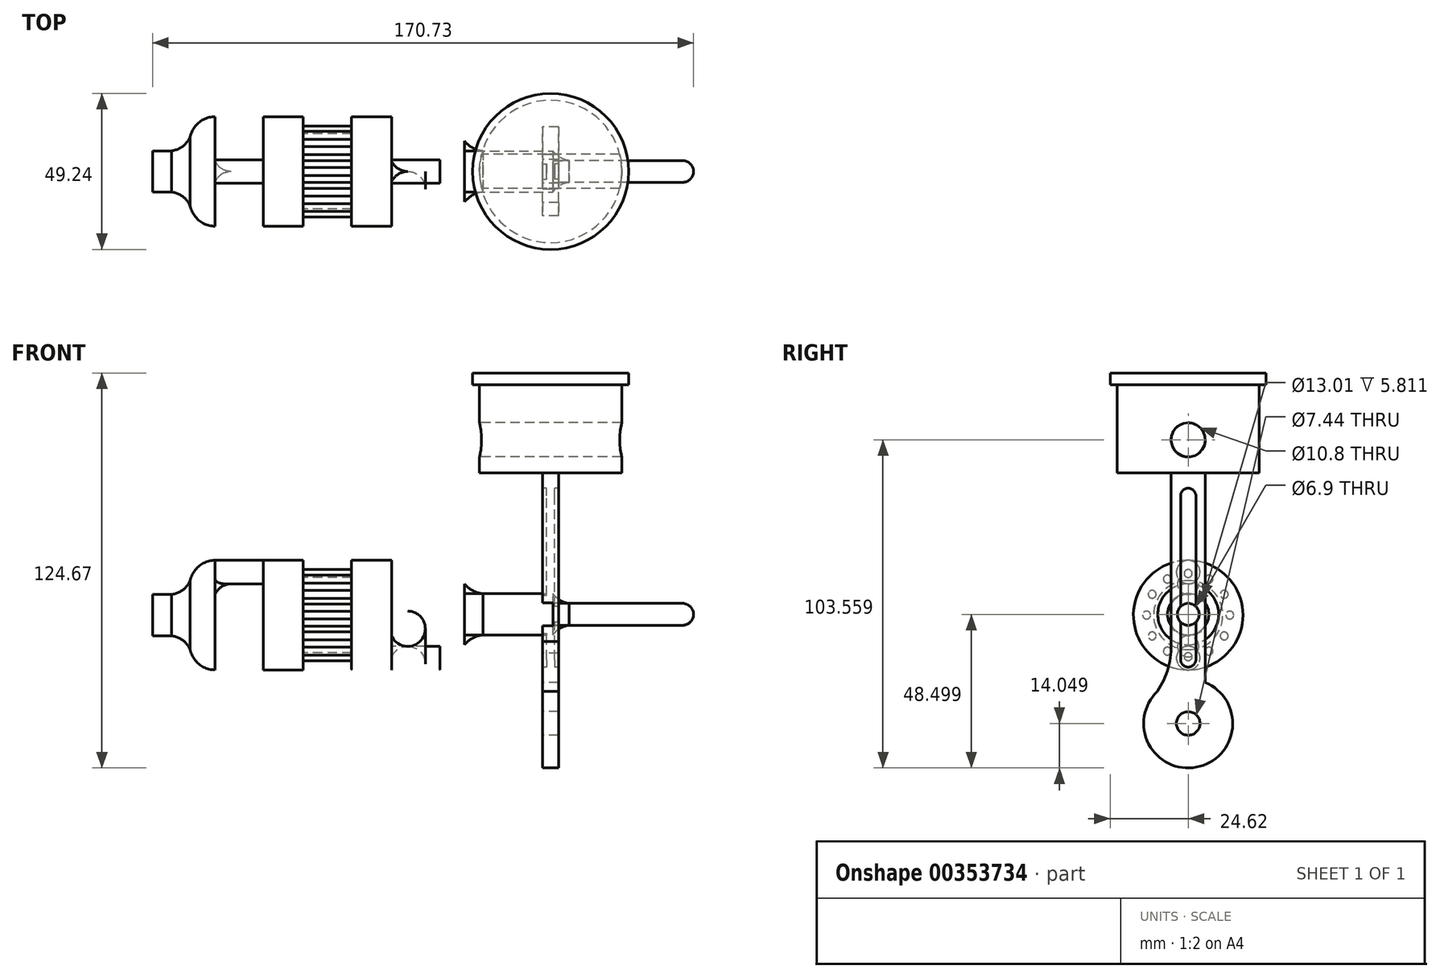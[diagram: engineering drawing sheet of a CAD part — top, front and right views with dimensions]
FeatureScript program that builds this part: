
annotation { "Feature Type Name" : "Feature", "Feature Type Description" : "" }
export const myFeature = defineFeature(function(context is Context, id is Id, definition is map)
    precondition{}
    {
        {
            var Q0;
            Q0=qCreatedBy(makeId("Front.planeOp"),FACE);
            var sketch = newSketch(context, id + "F0", { "sketchPlane" : qUnion([Q0])});
            skLineSegment(sketch, "E0.left", {"start": v(-105.92, 17.28) * mm, "end": v(-105.92, -17.28) * mm});
            skLineSegment(sketch, "E0.right", {"start": v(-113.74, 10.9) * mm, "end": v(-113.74, -10.9) * mm});
            skPoint(sketch, "E0.middle", {"position": v(-109.83, 0) * mm});
            skLineSegment(sketch, "E1.bottom", {"start": v(-113.74, 6.5) * mm, "end": v(-125.64, 6.5) * mm});
            skLineSegment(sketch, "E1.top", {"start": v(-113.74, -6.5) * mm, "end": v(-125.64, -6.5) * mm});
            skLineSegment(sketch, "E1.left", {"start": v(-113.74, 6.5) * mm, "end": v(-113.74, -6.5) * mm});
            skLineSegment(sketch, "E1.right", {"start": v(-125.64, 6.5) * mm, "end": v(-125.64, -6.5) * mm});
            skPoint(sketch, "E1.middle", {"position": v(-119.69, 0) * mm});
            skPoint(sketch, "E1.middle.positionSnap0", {"position": v(-113.74, 0) * mm});
            skPoint(sketch, "E1.centerSnap0", {"position": v(-113.74, 0) * mm});
            skLineSegment(sketch, "E2.bottom", {"start": v(-105.92, 17.28) * mm, "end": v(-90.68, 17.28) * mm});
            skLineSegment(sketch, "E2.top", {"start": v(-105.92, 9.85) * mm, "end": v(-90.68, 9.85) * mm});
            skLineSegment(sketch, "E2.left", {"start": v(-105.92, 17.28) * mm, "end": v(-105.92, 9.85) * mm});
            skLineSegment(sketch, "E2.right", {"start": v(-90.68, 17.28) * mm, "end": v(-90.68, 9.85) * mm});
            skPoint(sketch, "E2.middle", {"position": v(-98.3, 13.57) * mm});
            skLineSegment(sketch, "E3.bottom", {"start": v(-90.68, 17.28) * mm, "end": v(-78.06, 17.28) * mm});
            skLineSegment(sketch, "E3.top", {"start": v(-90.68, -17.28) * mm, "end": v(-78.06, -17.28) * mm});
            skLineSegment(sketch, "E3.left", {"start": v(-90.68, 17.28) * mm, "end": v(-90.68, -17.28) * mm});
            skLineSegment(sketch, "E3.right", {"start": v(-78.06, 17.28) * mm, "end": v(-78.06, -17.28) * mm});
            skPoint(sketch, "E3.middle", {"position": v(-84.37, 0) * mm});
            skLineSegment(sketch, "E4.bottom", {"start": v(-78.06, 3.45) * mm, "end": v(-62.82, 3.45) * mm});
            skLineSegment(sketch, "E4.top", {"start": v(-78.06, -3.98) * mm, "end": v(-62.82, -3.98) * mm});
            skLineSegment(sketch, "E4.left", {"start": v(-78.06, 3.45) * mm, "end": v(-78.06, -3.98) * mm});
            skLineSegment(sketch, "E4.right", {"start": v(-62.82, 3.45) * mm, "end": v(-62.82, -3.98) * mm});
            skPoint(sketch, "E4.middle", {"position": v(-70.44, -0.27) * mm});
            skLineSegment(sketch, "E5.right", {"start": v(-62.82, 17.28) * mm, "end": v(-62.82, 9.85) * mm});
            skLineSegment(sketch, "E6.bottom", {"start": v(-62.82, 17.28) * mm, "end": v(-50.23, 17.28) * mm});
            skLineSegment(sketch, "E6.top", {"start": v(-62.82, -17.28) * mm, "end": v(-50.23, -17.28) * mm});
            skLineSegment(sketch, "E6.left", {"start": v(-62.82, 17.28) * mm, "end": v(-62.82, -17.28) * mm});
            skLineSegment(sketch, "E6.right", {"start": v(-50.23, 17.28) * mm, "end": v(-50.23, -17.28) * mm});
            skPoint(sketch, "E6.middle", {"position": v(-56.53, 0) * mm});
            skLineSegment(sketch, "E7.bottom", {"start": v(-50.23, -9.85) * mm, "end": v(-34.94, -9.85) * mm});
            skLineSegment(sketch, "E7.top", {"start": v(-50.23, -17.28) * mm, "end": v(-34.94, -17.28) * mm});
            skLineSegment(sketch, "E7.left", {"start": v(-50.23, -9.85) * mm, "end": v(-50.23, -17.28) * mm});
            skPoint(sketch, "E7.middle", {"position": v(-42.59, -13.57) * mm});
            skLineSegment(sketch, "E8.bottom", {"start": v(-27.13, 6.75) * mm, "end": v(0.74, 6.75) * mm});
            skLineSegment(sketch, "E8.top", {"start": v(-27.13, -6.26) * mm, "end": v(0.74, -6.26) * mm});
            skLineSegment(sketch, "E8.right", {"start": v(0.74, 6.75) * mm, "end": v(0.74, -6.26) * mm});
            skPoint(sketch, "E8.middle", {"position": v(-13.2, 0.25) * mm});
            skLineSegment(sketch, "E9.left", {"start": v(0.74, 3.7) * mm, "end": v(0.74, -3.2) * mm});
            skLineSegment(sketch, "E10.left", {"start": v(-27.13, 10.99) * mm, "end": v(-27.13, -10.99) * mm});
            skLineSegment(sketch, "E10.right", {"start": v(-34.94, 17.28) * mm, "end": v(-34.94, -17.28) * mm});
            skPoint(sketch, "E10.middle", {"position": v(-31.04, 0) * mm});
            skPoint(sketch, "E11.middle.positionSnap0", {"position": v(-34.94, 0) * mm});
            skPoint(sketch, "E11.centerSnap0", {"position": v(-34.94, 0) * mm});
            skLineSegment(sketch, "E12.left", {"start": v(-27.13, 10.99) * mm, "end": v(-27.13, 9.85) * mm});
            skLineSegment(sketch, "E13", {"start": v(-105.92, 0) * mm, "end": v(-125.64, 0) * mm});
            skLineSegment(sketch, "E14", {"start": v(-105.92, 13.57) * mm, "end": v(-90.68, 13.57) * mm});
            skLineSegment(sketch, "E15", {"start": v(-90.68, 0) * mm, "end": v(-78.06, 0) * mm});
            skLineSegment(sketch, "E16", {"start": v(-78.06, 0) * mm, "end": v(-50.23, 0) * mm});
            skLineSegment(sketch, "E17", {"start": v(-50.23, -13.57) * mm, "end": v(-34.94, -13.57) * mm});
            skLineSegment(sketch, "E18", {"start": v(-13.2, 0.25) * mm, "end": v(0.74, 0.25) * mm});
            skLineSegment(sketch, "E19", {"start": v(-27.13, 0) * mm, "end": v(-31.04, 0) * mm});
            skLineSegment(sketch, "E20", {"start": v(-34.94, 0) * mm, "end": v(-31.04, 0) * mm});
            skLineSegment(sketch, "E21", {"start": v(-13.2, 0.25) * mm, "end": v(-27.13, 0.25) * mm});
            skLineSegment(sketch, "E22.bottom", {"start": v(0.74, 3.7) * mm, "end": v(41.64, 3.7) * mm});
            skLineSegment(sketch, "E22.top", {"start": v(0.74, -3.2) * mm, "end": v(41.64, -3.2) * mm});
            skLineSegment(sketch, "E22.right", {"start": v(41.64, 3.7) * mm, "end": v(41.64, -3.2) * mm});
            skPoint(sketch, "E22.middle", {"position": v(21.2, 0.25) * mm});
            skLineSegment(sketch, "E23", {"start": v(0.74, 0.25) * mm, "end": v(21.2, 0.25) * mm});
            skLineSegment(sketch, "E24", {"start": v(21.2, 0.25) * mm, "end": v(41.64, 0.25) * mm});
            skLineSegment(sketch, "E25.bottom", {"start": v(-95.76, 9.85) * mm, "end": v(-100.84, 9.85) * mm});
            skLineSegment(sketch, "E25.top", {"start": v(-95.76, 17.28) * mm, "end": v(-100.84, 17.28) * mm});
            skLineSegment(sketch, "E25.left", {"start": v(-95.76, 9.85) * mm, "end": v(-95.76, 17.28) * mm});
            skLineSegment(sketch, "E25.right", {"start": v(-100.84, 9.85) * mm, "end": v(-100.84, 17.28) * mm});
            skLineSegment(sketch, "E26.bottom", {"start": v(-40.05, -17.28) * mm, "end": v(-45.13, -17.28) * mm});
            skLineSegment(sketch, "E26.top", {"start": v(-40.05, -9.85) * mm, "end": v(-45.13, -9.85) * mm});
            skLineSegment(sketch, "E26.left", {"start": v(-40.05, -17.28) * mm, "end": v(-40.05, -9.85) * mm});
            skLineSegment(sketch, "E26.right", {"start": v(-45.13, -17.28) * mm, "end": v(-45.13, -9.85) * mm});
            skArc(sketch, "E27", {"start": v(-100.84, 9.85) * mm, "mid": v(-103.88, 8.94) * mm, "end": v(-105.92, 6.5) * mm});
            skLineSegment(sketch, "E28", {"start": v(-98.3, 9.85) * mm, "end": v(-98.3, 17.28) * mm});
            skArc(sketch, "E29.MirrorCS", {"start": v(-95.76, 9.85) * mm, "mid": v(-92.72, 8.94) * mm, "end": v(-90.68, 6.5) * mm});
            skArc(sketch, "E30", {"start": v(-50.23, -6.5) * mm, "mid": v(-48.18, -8.94) * mm, "end": v(-45.13, -9.85) * mm});
            skLineSegment(sketch, "E31", {"start": v(-42.59, -17.28) * mm, "end": v(-42.59, -9.85) * mm});
            skArc(sketch, "E32.MirrorCS", {"start": v(-34.94, -6.5) * mm, "mid": v(-37, -8.94) * mm, "end": v(-40.05, -9.85) * mm});
            skLineSegment(sketch, "E33", {"start": v(-78.06, -0.27) * mm, "end": v(-62.82, -0.27) * mm});
            skArc(sketch, "E34", {"start": v(-27.13, 9.85) * mm, "mid": v(-24.56, 7.69) * mm, "end": v(-21.32, 6.75) * mm});
            skArc(sketch, "E35.MirrorCS", {"start": v(-27.13, -9.35) * mm, "mid": v(-24.56, -7.19) * mm, "end": v(-21.32, -6.26) * mm});
            skArc(sketch, "E36", {"start": v(0.74, 6.75) * mm, "mid": v(2.97, 4.68) * mm, "end": v(5.86, 3.7) * mm});
            skArc(sketch, "E37", {"start": v(-119.69, 6.5) * mm, "mid": v(-116.13, 7.91) * mm, "end": v(-113.74, 10.9) * mm});
            skArc(sketch, "E38", {"start": v(-105.92, 17.28) * mm, "mid": v(-110.97, 15.49) * mm, "end": v(-113.74, 10.9) * mm});
            skArc(sketch, "E39.MirrorCS", {"start": v(-34.94, 17.28) * mm, "mid": v(-29.9, 15.48) * mm, "end": v(-27.12, 10.9) * mm});
            skPoint(sketch, "E40.orphan", {"position": v(-113.74, 17.28) * mm});
            skPoint(sketch, "E41.orphan", {"position": v(-27.13, 17.28) * mm});
            skArc(sketch, "E42.MirrorCS", {"start": v(-105.92, -17.28) * mm, "mid": v(-110.97, -15.49) * mm, "end": v(-113.74, -10.9) * mm});
            skArc(sketch, "E43.MirrorCS", {"start": v(-34.94, -17.28) * mm, "mid": v(-29.9, -15.48) * mm, "end": v(-27.12, -10.9) * mm});
            skPoint(sketch, "E44.orphan", {"position": v(-113.74, -17.28) * mm});
            skPoint(sketch, "E45.orphan", {"position": v(-27.13, -17.28) * mm});
            skLineSegment(sketch, "E46.bottom", {"start": v(-78.06, 14.38) * mm, "end": v(-62.82, 14.38) * mm});
            skLineSegment(sketch, "E46.top", {"start": v(-78.06, 11.89) * mm, "end": v(-62.82, 11.89) * mm});
            skLineSegment(sketch, "E46.left", {"start": v(-78.06, 14.38) * mm, "end": v(-78.06, 11.89) * mm});
            skLineSegment(sketch, "E46.right", {"start": v(-62.82, 14.38) * mm, "end": v(-62.82, 11.89) * mm});
            skLineSegment(sketch, "E47", {"start": v(-78.06, 13.13) * mm, "end": v(-62.82, 13.13) * mm});
            skArc(sketch, "E48", {"start": v(41.64, 3.7) * mm, "mid": v(45.09, 0.25) * mm, "end": v(41.64, -3.2) * mm});
            skLineSegment(sketch, "E49", {"start": v(41.64, 0.25) * mm, "end": v(45.09, 0.25) * mm});
            skSolve(sketch);
        }
        {
            var Q0;
            {var subQ0=sQuery(id+"F0.wireOp",EDGE,"E1.bottom");Q0=makeQuery(id+"F0.imprint","IMPRINT",FACE,{"disambiguationData":[TD([[makeQuery(id+"F0.imprint","IMPRINT",EDGE,{"derivedFrom":subQ0}),1.0]])]});}
            var Q1;
            {var subQ5=sQuery(id+"F0.wireOp",EDGE,"E0.bottom");Q1=makeQuery(id+"F0.imprint","IMPRINT",FACE,{"disambiguationData":[TD([[makeQuery(id+"F0.imprint","IMPRINT",EDGE,{"derivedFrom":subQ5}),1.0]])]});}
            var Q2;
            Q2=sQuery(id+"F0.wireOp",EDGE,"E13");
            revolve(context, id + "F1", {"entities" : qUnion([Q0, Q1]), "axis" : qUnion([Q2]), "revolveType" : RevolveType.FULL});
        }
        {
            var Q0;
            {var subQ0=sQuery(id+"F0.wireOp",EDGE,"E2.bottom");Q0=makeQuery(id+"F0.imprint","IMPRINT",FACE,{"disambiguationData":[TD([[makeQuery(id+"F0.imprint","IMPRINT",EDGE,{"derivedFrom":subQ0}),-1.0]])]});}
            var Q1;
            {var subQ5=sQuery(id+"F0.wireOp",EDGE,"E25.top");Q1=makeQuery(id+"F0.imprint","IMPRINT",FACE,{"disambiguationData":[TD([[makeQuery(id+"F0.imprint","IMPRINT",EDGE,{"derivedFrom":subQ5}),1.0]])]});}
            var Q2;
            Q2=sQuery(id+"F0.wireOp",EDGE,"E14");
            revolve(context, id + "F2", {"operationType" : NewBodyOperationType.ADD, "entities" : qUnion([Q0, Q1]), "axis" : qUnion([Q2]), "revolveType" : RevolveType.FULL});
        }
        {
            var Q0;
            {var subQ4=sQuery(id+"F0.wireOp",EDGE,"E3.bottom");Q0=makeQuery(id+"F0.imprint","IMPRINT",FACE,{"disambiguationData":[TD([[makeQuery(id+"F0.imprint","IMPRINT",EDGE,{"derivedFrom":subQ4}),-1.0]])]});}
            var Q1;
            {var subQ0=sQuery(id+"F0.wireOp",EDGE,"E4.bottom");Q1=makeQuery(id+"F0.imprint","IMPRINT",FACE,{"disambiguationData":[TD([[makeQuery(id+"F0.imprint","IMPRINT",EDGE,{"derivedFrom":subQ0}),-1.0]])]});}
            var Q2;
            {var subQ1=sQuery(id+"F0.wireOp",EDGE,"E6.bottom");Q2=makeQuery(id+"F0.imprint","IMPRINT",FACE,{"disambiguationData":[TD([[makeQuery(id+"F0.imprint","IMPRINT",EDGE,{"derivedFrom":subQ1}),-1.0]])]});}
            var Q3;
            Q3=sQuery(id+"F0.wireOp",EDGE,"E15");
            revolve(context, id + "F3", {"operationType" : NewBodyOperationType.ADD, "entities" : qUnion([Q0, Q1, Q2]), "axis" : qUnion([Q3]), "revolveType" : RevolveType.FULL});
        }
        {
            var Q0;
            {var subQ0=sQuery(id+"F0.wireOp",EDGE,"E7.bottom");Q0=makeQuery(id+"F0.imprint","IMPRINT",FACE,{"disambiguationData":[TD([[makeQuery(id+"F0.imprint","IMPRINT",EDGE,{"derivedFrom":subQ0}),-1.0]])]});}
            var Q1;
            {var subQ5=sQuery(id+"F0.wireOp",EDGE,"E26.top");Q1=makeQuery(id+"F0.imprint","IMPRINT",FACE,{"disambiguationData":[TD([[makeQuery(id+"F0.imprint","IMPRINT",EDGE,{"derivedFrom":subQ5}),1.0]])]});}
            var Q2;
            Q2=sQuery(id+"F0.wireOp",EDGE,"E17");
            revolve(context, id + "F4", {"operationType" : NewBodyOperationType.ADD, "entities" : qUnion([Q0, Q1]), "axis" : qUnion([Q2]), "revolveType" : RevolveType.FULL});
        }
        {
            var Q0;
            {var subQ5=sQuery(id+"F0.wireOp",EDGE,"E38");Q0=makeQuery(id+"F0.imprint","IMPRINT",FACE,{"disambiguationData":[TD([[makeQuery(id+"F0.imprint","IMPRINT",EDGE,{"derivedFrom":subQ5}),1.0]])]});}
            var Q1;
            {var subQ4=sQuery(id+"F0.wireOp",EDGE,"E12.left");Q1=makeQuery(id+"F0.imprint","IMPRINT",FACE,{"disambiguationData":[TD([[makeQuery(id+"F0.imprint","IMPRINT",EDGE,{"derivedFrom":subQ4}),-1.0]])]});}
            var Q2;
            Q2=sQuery(id+"F0.wireOp",EDGE,"E20");
            revolve(context, id + "F5", {"entities" : qUnion([Q0, Q1]), "axis" : qUnion([Q2]), "revolveType" : RevolveType.FULL});
        }
        {
            var Q0;
            {var subQ2=sQuery(id+"F0.wireOp",EDGE,"E22.bottom");Q0=makeQuery(id+"F0.imprint","IMPRINT",FACE,{"disambiguationData":[TD([[makeQuery(id+"F0.imprint","IMPRINT",EDGE,{"derivedFrom":subQ2}),-1.0]])]});}
            var Q1;
            Q1=sQuery(id+"F0.wireOp",EDGE,"E23");
            revolve(context, id + "F6", {"entities" : qUnion([Q0]), "axis" : qUnion([Q1]), "revolveType" : RevolveType.FULL});
        }
        {
            var Q0;
            {var subQ1=sQuery(id+"F0.wireOp",EDGE,"E8.bottom");Q0=makeQuery(id+"F0.imprint","IMPRINT",FACE,{"disambiguationData":[TD([[makeQuery(id+"F0.imprint","IMPRINT",EDGE,{"derivedFrom":subQ1}),-1.0]])]});}
            var Q1;
            Q1=sQuery(id+"F0.wireOp",EDGE,"E21");
            revolve(context, id + "F7", {"entities" : qUnion([Q0]), "axis" : qUnion([Q1]), "revolveType" : RevolveType.FULL});
        }
        {
            var Q0;
            Q0=qCreatedBy(makeId("Right.planeOp"),FACE);
            var sketch = newSketch(context, id + "F8", { "sketchPlane" : qUnion([Q0])});
            skCircle(sketch, "E50", {"center": v(0, -34.2) * mm, "radius": 14.04 * mm});
            skLineSegment(sketch, "E51.top", {"start": v(5.43, 44.88) * mm, "end": v(-5.43, 44.88) * mm});
            skLineSegment(sketch, "E51.left", {"start": v(5.43, -21.25) * mm, "end": v(5.43, 44.88) * mm});
            skLineSegment(sketch, "E51.right", {"start": v(-5.43, -21.25) * mm, "end": v(-5.43, 44.88) * mm});
            skPoint(sketch, "E51.middle", {"position": v(0, 11.82) * mm});
            skArc(sketch, "E52", {"start": v(-9.78, -24.12) * mm, "mid": v(-6.23, -16.62) * mm, "end": v(-5.43, -8.37) * mm});
            skArc(sketch, "E53.MirrorCS", {"start": v(9.78, -24.12) * mm, "mid": v(6.23, -16.62) * mm, "end": v(5.43, -8.37) * mm});
            skLineSegment(sketch, "E54.bottom", {"start": v(22.46, 44.88) * mm, "end": v(-22.46, 44.88) * mm});
            skLineSegment(sketch, "E54.top", {"start": v(22.46, 72.74) * mm, "end": v(-22.46, 72.74) * mm});
            skLineSegment(sketch, "E54.left", {"start": v(22.46, 44.88) * mm, "end": v(22.46, 72.74) * mm});
            skLineSegment(sketch, "E54.right", {"start": v(-22.46, 44.88) * mm, "end": v(-22.46, 72.74) * mm});
            skPoint(sketch, "E54.middle", {"position": v(0, 58.81) * mm});
            skLineSegment(sketch, "E55.bottom", {"start": v(24.62, 72.74) * mm, "end": v(-24.62, 72.74) * mm});
            skLineSegment(sketch, "E55.top", {"start": v(24.62, 76.42) * mm, "end": v(-24.62, 76.42) * mm});
            skLineSegment(sketch, "E55.left", {"start": v(24.62, 72.74) * mm, "end": v(24.62, 76.42) * mm});
            skLineSegment(sketch, "E55.right", {"start": v(-24.62, 72.74) * mm, "end": v(-24.62, 76.42) * mm});
            skPoint(sketch, "E55.middle", {"position": v(0, 74.58) * mm});
            skPoint(sketch, "E55.middle.positionSnap0", {"position": v(0, 72.74) * mm});
            skPoint(sketch, "E55.centerSnap0", {"position": v(0, 72.74) * mm});
            skArc(sketch, "E56", {"start": v(-24.62, 72.74) * mm, "mid": v(-24.07, 69.07) * mm, "end": v(-22.46, 65.72) * mm});
            skArc(sketch, "E57.MirrorCS", {"start": v(24.62, 72.74) * mm, "mid": v(24.07, 69.07) * mm, "end": v(22.46, 65.72) * mm});
            skLineSegment(sketch, "E58.left", {"start": v(2.42, -14) * mm, "end": v(2.42, 37.63) * mm});
            skLineSegment(sketch, "E58.right", {"start": v(-2.42, -14) * mm, "end": v(-2.42, 37.63) * mm});
            skArc(sketch, "E59", {"start": v(2.42, 37.63) * mm, "mid": v(0, 40.05) * mm, "end": v(-2.42, 37.63) * mm});
            skArc(sketch, "E60", {"start": v(2.42, -14) * mm, "mid": v(0, -16.42) * mm, "end": v(-2.42, -14) * mm});
            skCircle(sketch, "E61", {"center": v(0, 55.3) * mm, "radius": 5.4 * mm});
            skLineSegment(sketch, "E62", {"start": v(0, 44.88) * mm, "end": v(0, 49.9) * mm});
            skLineSegment(sketch, "E63", {"start": v(0, 60.71) * mm, "end": v(0, 76.42) * mm});
            skCircle(sketch, "E64", {"center": v(0, -34.2) * mm, "radius": 3.72 * mm});
            skSolve(sketch);
        }
        {
            var Q0;
            {var subQ6=sQuery(id+"F8.wireOp",EDGE,"E54.bottom");var subQ7=sQuery(id+"F8.wireOp",EDGE,"E51.left");var subQ8=makeQuery(id+"F8.imprint","INTERSECT",VERTEX,{"derivedFrom":[subQ7,subQ6]});Q0=makeQuery(id+"F8.imprint","IMPRINT",FACE,{"disambiguationData":[TD([[makeQuery(id+"F8.imprint","IMPRINT",EDGE,{"disambiguationData":[TD([[subQ8,1.0]])],"derivedFrom":subQ7}),1.0]])]});}
            var Q1;
            {var subQ1=sQuery(id+"F8.wireOp",EDGE,"E50");var subQ3=sQuery(id+"F8.wireOp",EDGE,"E52");var subQ4=makeQuery(id+"F8.imprint","INTERSECT",VERTEX,{"derivedFrom":[subQ1,subQ3]});Q1=makeQuery(id+"F8.imprint","IMPRINT",FACE,{"disambiguationData":[TD([[makeQuery(id+"F8.imprint","IMPRINT",EDGE,{"disambiguationData":[TD([[subQ4,-1.0]])],"derivedFrom":subQ3}),-1.0]])]});}
            var Q2;
            {var subQ1=sQuery(id+"F8.wireOp",EDGE,"E50");var subQ3=sQuery(id+"F8.wireOp",EDGE,"E53.MirrorCS");var subQ4=makeQuery(id+"F8.imprint","INTERSECT",VERTEX,{"derivedFrom":[subQ1,subQ3]});Q2=makeQuery(id+"F8.imprint","IMPRINT",FACE,{"disambiguationData":[TD([[makeQuery(id+"F8.imprint","IMPRINT",EDGE,{"disambiguationData":[TD([[subQ4,-1.0]])],"derivedFrom":subQ3}),1.0]])]});}
            var Q3;
            {var subQ3=sQuery(id+"F8.wireOp",EDGE,"tyP9yjyq-YdZF-iyVl-qhYa-RC6tVWskorja");var subQ4=sQuery(id+"F8.wireOp",EDGE,"jZ58i1hO-h05t-zmx4-ybOM-HXGDdQZZOhNS");var subQ5=makeQuery(id+"F8.imprint","INTERSECT",VERTEX,{"disambiguationData":[OD(0.0)],"derivedFrom":[subQ4,subQ3]});Q3=makeQuery(id+"F8.imprint","IMPRINT",FACE,{"disambiguationData":[TD([[makeQuery(id+"F8.imprint","IMPRINT",EDGE,{"disambiguationData":[TD([[subQ5,-1.0]])],"derivedFrom":subQ4}),-1.0]])]});}
            var Q4;
            Q4=makeQuery(id+"F8.imprint","IMPRINT",FACE,{"disambiguationData":[TD([[makeQuery(id+"F8.imprint","IMPRINT",EDGE,{"derivedFrom":sQuery(id+"F8.wireOp",EDGE,"E64")}),-1.0]])]});
            extrude(context, id + "F9", {"entities" : qUnion([Q0, Q1, Q2, Q3, Q4]), "endBound" : BoundingType.SYMMETRIC, "depth" : 5.08 * mm});
        }
        {
            var Q0;
            {var subQ0=sQuery(id+"F8.wireOp",EDGE,"E55.left");Q0=makeQuery(id+"F8.imprint","IMPRINT",FACE,{"disambiguationData":[TD([[makeQuery(id+"F8.imprint","IMPRINT",EDGE,{"derivedFrom":subQ0}),1.0]])]});}
            var Q1;
            {var subQ3=sQuery(id+"F8.wireOp",EDGE,"E57.MirrorCS");Q1=makeQuery(id+"F8.imprint","IMPRINT",FACE,{"disambiguationData":[TD([[makeQuery(id+"F8.imprint","IMPRINT",EDGE,{"derivedFrom":subQ3}),-1.0]])]});}
            var Q2;
            {var subQ5=sQuery(id+"F8.wireOp",EDGE,"E62");Q2=makeQuery(id+"F8.imprint","IMPRINT",FACE,{"disambiguationData":[TD([[makeQuery(id+"F8.imprint","IMPRINT",EDGE,{"derivedFrom":subQ5}),-1.0]])]});}
            var Q3;
            Q3=sQuery(id+"F8.wireOp",EDGE,"E63");
            revolve(context, id + "F10", {"operationType" : NewBodyOperationType.ADD, "entities" : qUnion([Q0, Q1, Q2]), "axis" : qUnion([Q3]), "revolveType" : RevolveType.FULL});
        }
        {
            var Q0;
            {var subQ0=sQuery(id+"F8.wireOp",EDGE,"E61");var subQ1=makeQuery(id+"F8.imprint","INTERSECT",VERTEX,{"derivedFrom":[subQ0,sQuery(id+"F8.wireOp",EDGE,"E62")]});Q0=makeQuery(id+"F8.imprint","IMPRINT",FACE,{"disambiguationData":[TD([[makeQuery(id+"F8.imprint","IMPRINT",EDGE,{"disambiguationData":[TD([[subQ1,1.0]])],"derivedFrom":subQ0}),1.0]])]});}
            extrude(context, id + "F11", {"entities" : qUnion([Q0]), "operationType" : NewBodyOperationType.REMOVE, "endBound" : BoundingType.SYMMETRIC, "depth" : 50.8 * mm});
        }
        {
            var Q0;
            Q0=makeQuery(id+"F8.imprint","IMPRINT",FACE,{"disambiguationData":[TD([[makeQuery(id+"F8.imprint","IMPRINT",EDGE,{"derivedFrom":sQuery(id+"F8.wireOp",EDGE,"E58.left")}),1.0]])]});
            extrude(context, id + "F12", {"entities" : qUnion([Q0]), "operationType" : NewBodyOperationType.ADD, "endBound" : BoundingType.SYMMETRIC, "depth" : 2.54 * mm});
        }
        {
            var Q0;
            {var subQ3=sQuery(id+"F0.wireOp",EDGE,"E27");Q0=makeQuery(id+"F0.imprint","IMPRINT",FACE,{"disambiguationData":[TD([[makeQuery(id+"F0.imprint","IMPRINT",EDGE,{"derivedFrom":subQ3}),-1.0]])]});}
            var Q1;
            {var subQ3=sQuery(id+"F0.wireOp",EDGE,"E29.MirrorCS");Q1=makeQuery(id+"F0.imprint","IMPRINT",FACE,{"disambiguationData":[TD([[makeQuery(id+"F0.imprint","IMPRINT",EDGE,{"derivedFrom":subQ3}),1.0]])]});}
            var Q2;
            Q2=sQuery(id+"F0.wireOp",EDGE,"E2.top");
            revolve(context, id + "F13", {"operationType" : NewBodyOperationType.ADD, "entities" : qUnion([Q0, Q1]), "axis" : qUnion([Q2]), "revolveType" : RevolveType.FULL});
        }
        {
            var Q0;
            {var subQ3=sQuery(id+"F0.wireOp",EDGE,"E32.MirrorCS");Q0=makeQuery(id+"F0.imprint","IMPRINT",FACE,{"disambiguationData":[TD([[makeQuery(id+"F0.imprint","IMPRINT",EDGE,{"derivedFrom":subQ3}),1.0]])]});}
            var Q1;
            {var subQ3=sQuery(id+"F0.wireOp",EDGE,"E30");Q1=makeQuery(id+"F0.imprint","IMPRINT",FACE,{"disambiguationData":[TD([[makeQuery(id+"F0.imprint","IMPRINT",EDGE,{"derivedFrom":subQ3}),-1.0]])]});}
            var Q2;
            Q2=sQuery(id+"F0.wireOp",EDGE,"E7.bottom");
            revolve(context, id + "F14", {"entities" : qUnion([Q0, Q1]), "axis" : qUnion([Q2]), "revolveType" : RevolveType.FULL});
        }
        {
            var Q0;
            {var subQ3=sQuery(id+"F0.wireOp",EDGE,"E34");Q0=makeQuery(id+"F0.imprint","IMPRINT",FACE,{"disambiguationData":[TD([[makeQuery(id+"F0.imprint","IMPRINT",EDGE,{"derivedFrom":subQ3}),-1.0]])]});}
            var Q1;
            {var subQ0=sQuery(id+"F0.wireOp",EDGE,"E36");Q1=makeQuery(id+"F0.imprint","IMPRINT",FACE,{"disambiguationData":[TD([[makeQuery(id+"F0.imprint","IMPRINT",EDGE,{"derivedFrom":subQ0}),-1.0]])]});}
            var Q2;
            Q2=sQuery(id+"F0.wireOp",EDGE,"E21");
            revolve(context, id + "F15", {"entities" : qUnion([Q0, Q1]), "axis" : qUnion([Q2]), "revolveType" : RevolveType.FULL});
        }
        {
            var Q0;
            {var subQ3=sQuery(id+"F0.wireOp",EDGE,"E37");Q0=makeQuery(id+"F0.imprint","IMPRINT",FACE,{"disambiguationData":[TD([[makeQuery(id+"F0.imprint","IMPRINT",EDGE,{"derivedFrom":subQ3}),-1.0]])]});}
            var Q1;
            Q1=sQuery(id+"F0.wireOp",EDGE,"E13");
            revolve(context, id + "F16", {"operationType" : NewBodyOperationType.ADD, "entities" : qUnion([Q0]), "axis" : qUnion([Q1]), "revolveType" : RevolveType.FULL});
        }
        {
            var Q0;
            {var subQ0=sQuery(id+"F0.wireOp",EDGE,"E46.bottom");Q0=makeQuery(id+"F0.imprint","IMPRINT",FACE,{"disambiguationData":[TD([[makeQuery(id+"F0.imprint","IMPRINT",EDGE,{"derivedFrom":subQ0}),-1.0]])]});}
            var Q1;
            Q1=sQuery(id+"F0.wireOp",EDGE,"E47");
            revolve(context, id + "F17", {"operationType" : NewBodyOperationType.ADD, "entities" : qUnion([Q0]), "axis" : qUnion([Q1]), "revolveType" : RevolveType.FULL});
        }
        {
            var Q0;
            Q0=makeQuery(id+"F17.opRevolve","SWEPT_FACE",FACE,{"disambiguationData":[OSD([sQuery(id+"F0.wireOp",EDGE,"E46.bottom")])]});
            var Q1;
            Q1=sQuery(id+"F0.wireOp",EDGE,"E16");
            circularPattern(context, id + "F18", {"patternType" : PatternType.FACE, "faces" : qUnion([Q0]), "axis" : qUnion([Q1]), "angle" : 360 * degree, "instanceCount" : 12, "equalSpace" : true});
        }
        {
            var Q0;
            {var subQ3=sQuery(id+"F0.wireOp",EDGE,"E49");Q0=makeQuery(id+"F0.imprint","IMPRINT",FACE,{"disambiguationData":[TD([[makeQuery(id+"F0.imprint","IMPRINT",EDGE,{"derivedFrom":subQ3}),1.0]])]});}
            var Q1;
            Q1=sQuery(id+"F0.wireOp",EDGE,"E49");
            revolve(context, id + "F19", {"operationType" : NewBodyOperationType.ADD, "entities" : qUnion([Q0]), "axis" : qUnion([Q1]), "revolveType" : RevolveType.FULL});
        }
    });
